# Revit family: NLRS_57_AIR_UN_plenum_linear-ceiling-grill-soooxx-for-srxr_2xD_return_LT_sacs
name_source: partatom
category: Air Terminals
units: mm (PartAtom-declared; Revit-internal decimal feet)

## family parameters
Always vertical = Yes
Cut with Voids When Loaded = No
Part Type = Normal
Room Calculation Point = Yes
Round Connector Dimension = Use Diameter
Shared = No
Work Plane-Based = No

## types (1)
- SOOOxx-special
    Assembly Code = 57.00
    Default Elevation = 2700 mm  [stored 8.85827 ft]
    Description = Solid Air plenum for line Diffuser
    Manufacturer = Solid Air Climate Solutions
    Max Flow = 0.0 L/s
    Min Flow = 0.0 L/s
    Model = Special plenums for SR
    NLRS_C_content_datum_gewijzigd = 11-03-2024
    NLRS_C_content_provider = Solid Air Climate Solutions
    NLRS_C_content_versie = 2.21.01
    NLRS_C_description = Solid Air plenum for line Diffuser
    Plenum_Material = NLRS_57_sendzimir verzinkt_gen_sacs
    SACS_Data_Hidden = SOOOxx_2xD
    SACS_Dummy = 1
    Type Comments = Special plenums for Line grill SR
    URL = https://solid-air.nl

note: [stored X ft] marks values corroborated as IEEE doubles in the binary element streams (Revit-internal decimal feet)

## geometry (parser evidence)
native form markers: Sweep x7
no freeform markers — native parametric forms only
